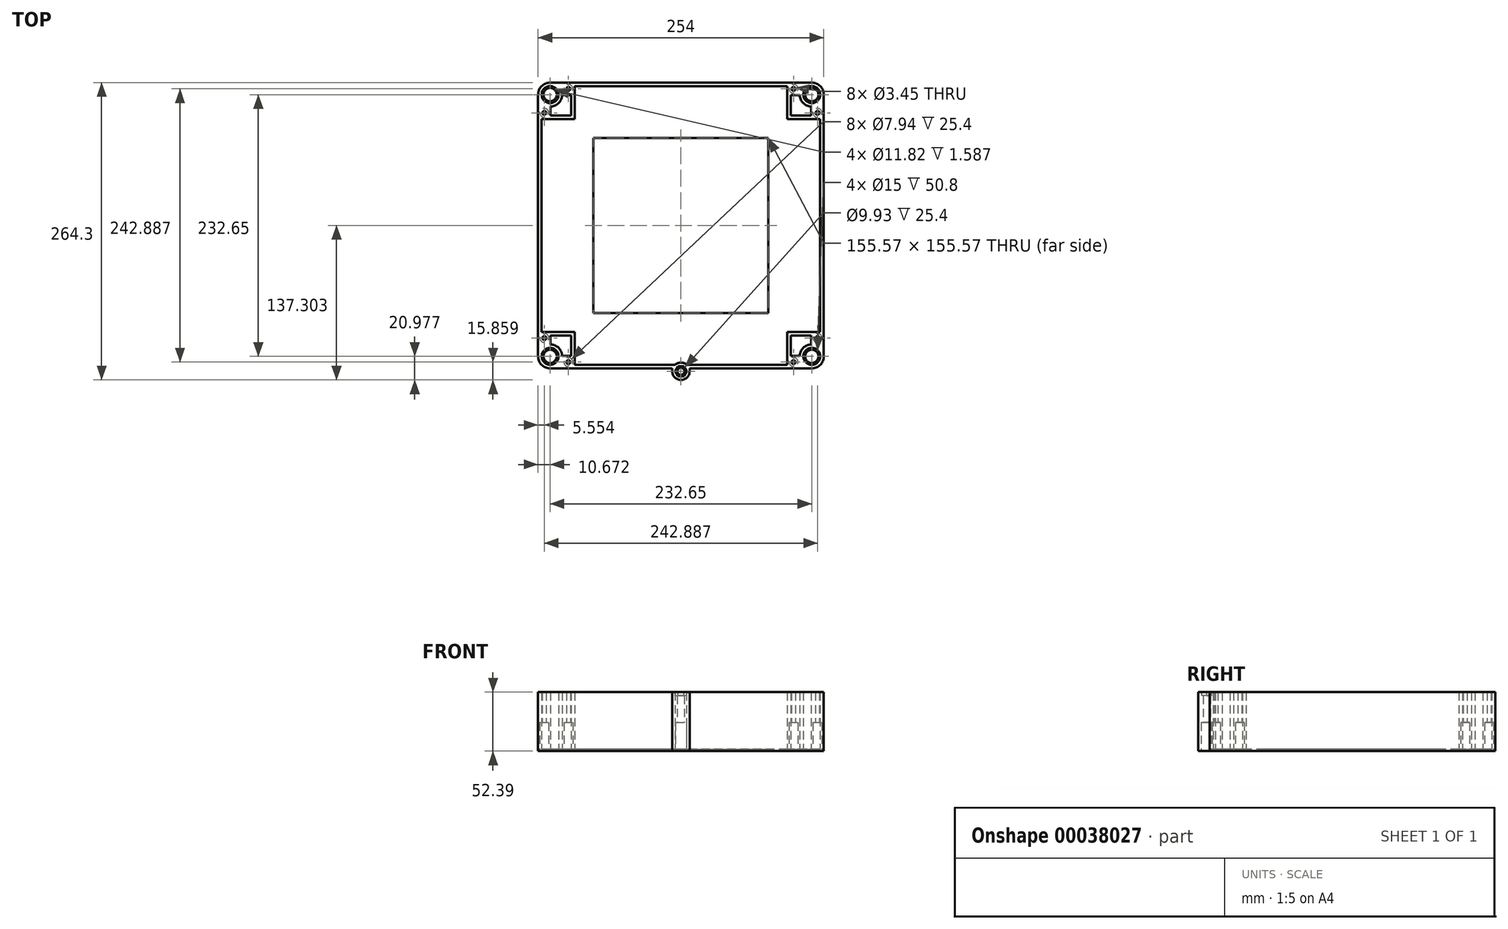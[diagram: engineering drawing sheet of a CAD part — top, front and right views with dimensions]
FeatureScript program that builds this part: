
annotation { "Feature Type Name" : "Feature", "Feature Type Description" : "" }
export const myFeature = defineFeature(function(context is Context, id is Id, definition is map)
    precondition{}
    {
        {
            var Q0;
            Q0=qCreatedBy(makeId("Top.planeOp"),FACE);
            var sketch = newSketch(context, id + "F0", { "sketchPlane" : qUnion([Q0])});
            skLineSegment(sketch, "E0.bottom", {"start": v(0, 0) * mm, "end": v(155.58, 0) * mm});
            skLineSegment(sketch, "E0.top", {"start": v(0, -155.58) * mm, "end": v(155.58, -155.58) * mm});
            skLineSegment(sketch, "E0.left", {"start": v(0, 0) * mm, "end": v(0, -155.58) * mm});
            skLineSegment(sketch, "E0.right", {"start": v(155.58, 0) * mm, "end": v(155.58, -155.58) * mm});
            skLineSegment(sketch, "E1", {"start": v(77.79, -155.58) * mm, "end": v(77.79, 0) * mm, "construction": true});
            skPoint(sketch, "E2.rect.middle", {"position": v(77.79, -77.79) * mm});
            skLineSegment(sketch, "E3.rect.bottom", {"start": v(204.79, 49.21) * mm, "end": v(-49.21, 49.21) * mm});
            skLineSegment(sketch, "E3.rect.top", {"start": v(204.79, -204.79) * mm, "end": v(-49.21, -204.79) * mm});
            skLineSegment(sketch, "E3.rect.left", {"start": v(204.79, 49.21) * mm, "end": v(204.79, -204.79) * mm});
            skLineSegment(sketch, "E3.rect.right", {"start": v(-49.21, 49.21) * mm, "end": v(-49.21, -204.79) * mm});
            skCircle(sketch, "E4", {"center": v(194.11, 38.54) * mm, "radius": 10.67 * mm, "construction": true});
            skCircle(sketch, "E5", {"center": v(-38.54, 38.54) * mm, "radius": 5.91 * mm});
            skCircle(sketch, "E6", {"center": v(-38.54, -194.11) * mm, "radius": 5.91 * mm});
            skCircle(sketch, "E7", {"center": v(194.11, -194.11) * mm, "radius": 5.91 * mm});
            skCircle(sketch, "E8", {"center": v(194.11, 38.54) * mm, "radius": 5.91 * mm});
            skLineSegment(sketch, "E9", {"start": v(77.79, 0) * mm, "end": v(77.79, 38.54) * mm, "construction": true});
            skLineSegment(sketch, "E10", {"start": v(194.11, 38.54) * mm, "end": v(194.11, 22.3) * mm, "construction": true});
            skLineSegment(sketch, "E11", {"start": v(194.11, 38.54) * mm, "end": v(177.88, 38.54) * mm, "construction": true});
            skLineSegment(sketch, "E12", {"start": v(177.88, 38.54) * mm, "end": v(-22.3, 38.54) * mm, "construction": true});
            skLineSegment(sketch, "E13", {"start": v(-22.3, 38.54) * mm, "end": v(-38.54, 38.54) * mm, "construction": true});
            skLineSegment(sketch, "E14", {"start": v(-38.54, 38.54) * mm, "end": v(-38.54, 22.3) * mm, "construction": true});
            skLineSegment(sketch, "E15", {"start": v(-38.54, 22.3) * mm, "end": v(-38.54, -177.88) * mm, "construction": true});
            skLineSegment(sketch, "E16", {"start": v(-38.54, -177.88) * mm, "end": v(-38.54, -194.11) * mm, "construction": true});
            skLineSegment(sketch, "E17", {"start": v(-38.54, -194.11) * mm, "end": v(-22.3, -194.11) * mm, "construction": true});
            skLineSegment(sketch, "E18", {"start": v(-22.3, -194.11) * mm, "end": v(177.88, -194.11) * mm, "construction": true});
            skLineSegment(sketch, "E19", {"start": v(177.88, -194.11) * mm, "end": v(194.11, -194.11) * mm, "construction": true});
            skLineSegment(sketch, "E20", {"start": v(194.11, -194.11) * mm, "end": v(194.11, -177.88) * mm, "construction": true});
            skLineSegment(sketch, "E21", {"start": v(194.11, -177.88) * mm, "end": v(194.11, 22.3) * mm, "construction": true});
            skLineSegment(sketch, "E22", {"start": v(194.11, 22.3) * mm, "end": v(199.23, 22.3) * mm, "construction": true});
            skLineSegment(sketch, "E23", {"start": v(177.88, 38.54) * mm, "end": v(177.88, 43.66) * mm, "construction": true});
            skLineSegment(sketch, "E24", {"start": v(-38.54, 22.3) * mm, "end": v(-43.66, 22.3) * mm, "construction": true});
            skLineSegment(sketch, "E25", {"start": v(-22.3, 38.54) * mm, "end": v(-22.3, 43.66) * mm, "construction": true});
            skLineSegment(sketch, "E26", {"start": v(-38.54, -177.88) * mm, "end": v(-43.66, -177.88) * mm, "construction": true});
            skLineSegment(sketch, "E27", {"start": v(-22.3, -194.11) * mm, "end": v(-22.3, -199.23) * mm, "construction": true});
            skLineSegment(sketch, "E28", {"start": v(177.88, -194.11) * mm, "end": v(177.88, -199.23) * mm, "construction": true});
            skLineSegment(sketch, "E29", {"start": v(194.11, -177.88) * mm, "end": v(199.23, -177.88) * mm, "construction": true});
            skCircle(sketch, "E30", {"center": v(-22.3, -199.23) * mm, "radius": 1.73 * mm});
            skCircle(sketch, "E31", {"center": v(-43.66, -177.88) * mm, "radius": 1.73 * mm});
            skCircle(sketch, "E32", {"center": v(177.88, -199.23) * mm, "radius": 1.73 * mm});
            skCircle(sketch, "E33", {"center": v(199.23, -177.88) * mm, "radius": 1.73 * mm});
            skCircle(sketch, "E34", {"center": v(199.23, 22.3) * mm, "radius": 1.73 * mm});
            skCircle(sketch, "E35", {"center": v(177.88, 43.66) * mm, "radius": 1.73 * mm});
            skCircle(sketch, "E36", {"center": v(-22.3, 43.66) * mm, "radius": 1.73 * mm});
            skCircle(sketch, "E37", {"center": v(-43.66, 22.3) * mm, "radius": 1.73 * mm});
            skLineSegment(sketch, "E38", {"start": v(77.79, -204.79) * mm, "end": v(77.79, -207.4) * mm, "construction": true});
            skLineSegment(sketch, "E39", {"start": v(70.1, -207.4) * mm, "end": v(85.48, -207.4) * mm, "construction": true});
            skCircle(sketch, "E40", {"center": v(77.79, -207.4) * mm, "radius": 3.18 * mm});
            skArc(sketch, "E41", {"start": v(85.48, -207.4) * mm, "mid": v(77.79, -199.7) * mm, "end": v(70.1, -207.4) * mm, "construction": true});
            skLineSegment(sketch, "E42", {"start": v(77.79, -204.79) * mm, "end": v(77.79, -199.7) * mm, "construction": true});
            skLineSegment(sketch, "E43", {"start": v(70.1, -207.4) * mm, "end": v(70.1, -204.79) * mm});
            skLineSegment(sketch, "E44", {"start": v(85.48, -207.4) * mm, "end": v(85.48, -204.79) * mm});
            skArc(sketch, "E45", {"start": v(70.1, -207.4) * mm, "mid": v(77.79, -215.1) * mm, "end": v(85.48, -207.4) * mm});
            skSolve(sketch);
        }
        {
            var Q0;
            Q0 = qSketchRegion(id + "F0", true);
            extrude(context, id + "F1", {"entities" : qUnion([Q0]), "depth" : 1.59 * mm});
        }
        {
            var Q0;
            Q0=makeQuery(id+"F1.opExtrude","CAP_FACE",FACE,{"disambiguationData":[OSD([sQuery(id+"F0.wireOp",EDGE,"E0.bottom"),sQuery(id+"F0.wireOp",EDGE,"E0.top"),sQuery(id+"F0.wireOp",EDGE,"E0.left"),sQuery(id+"F0.wireOp",EDGE,"E0.right"),sQuery(id+"F0.wireOp",EDGE,"E3.rect.bottom"),sQuery(id+"F0.wireOp",EDGE,"E3.rect.top"),sQuery(id+"F0.wireOp",EDGE,"E3.rect.left"),sQuery(id+"F0.wireOp",EDGE,"E3.rect.right"),sQuery(id+"F0.wireOp",EDGE,"E5"),sQuery(id+"F0.wireOp",EDGE,"E6"),sQuery(id+"F0.wireOp",EDGE,"E7"),sQuery(id+"F0.wireOp",EDGE,"E8"),sQuery(id+"F0.wireOp",EDGE,"43b1e4d8-dc6b-47d4-afa9-39d73305b24d"),sQuery(id+"F0.wireOp",EDGE,"f6cbb305-d163-4643-bee7-746698ecbea6"),sQuery(id+"F0.wireOp",EDGE,"d3adae85-02bf-45b9-a1e7-f1405657d824"),sQuery(id+"F0.wireOp",EDGE,"c2a7c8b4-6c69-4894-a4e0-b23b3878c01f"),sQuery(id+"F0.wireOp",EDGE,"fd5b1bc6-ad7d-40a0-8725-81bf3ed5f793"),sQuery(id+"F0.wireOp",EDGE,"3342989b-8784-4d44-b616-02abcfacb7a4"),sQuery(id+"F0.wireOp",EDGE,"51ad0ca2-9e39-4300-82ec-fa5dff985d1e"),sQuery(id+"F0.wireOp",EDGE,"bdff3714-a2b8-41a3-9f31-29bf1a054880")])],"isStart":false});
            var sketch = newSketch(context, id + "F2", { "sketchPlane" : qUnion([Q0])});
            skLineSegment(sketch, "E46.bottom", {"start": v(204.79, 49.21) * mm, "end": v(-49.21, 49.21) * mm});
            skLineSegment(sketch, "E46.top", {"start": v(204.79, -204.79) * mm, "end": v(-49.21, -204.79) * mm});
            skLineSegment(sketch, "E46.left", {"start": v(204.79, 49.21) * mm, "end": v(204.79, -204.79) * mm});
            skLineSegment(sketch, "E46.right", {"start": v(-49.21, 49.21) * mm, "end": v(-49.21, -204.79) * mm});
            skLineSegment(sketch, "E47.bottom", {"start": v(172.33, 46.04) * mm, "end": v(-16.75, 46.04) * mm});
            skLineSegment(sketch, "E47.left", {"start": v(172.33, 46.04) * mm, "end": v(172.33, 16.75) * mm});
            skLineSegment(sketch, "E47.right", {"start": v(-16.75, 46.04) * mm, "end": v(-16.75, 16.75) * mm});
            skLineSegment(sketch, "E48.bottom", {"start": v(201.61, 16.75) * mm, "end": v(172.33, 16.75) * mm});
            skLineSegment(sketch, "E48.top", {"start": v(201.61, -172.33) * mm, "end": v(172.33, -172.33) * mm});
            skLineSegment(sketch, "E48.left", {"start": v(201.61, 16.75) * mm, "end": v(201.61, -172.33) * mm});
            skLineSegment(sketch, "E49", {"start": v(199.23, 22.3) * mm, "end": v(199.23, 16.75) * mm, "construction": true});
            skLineSegment(sketch, "E50", {"start": v(177.88, 43.66) * mm, "end": v(172.33, 43.66) * mm, "construction": true});
            skLineSegment(sketch, "E51", {"start": v(204.79, -77.79) * mm, "end": v(201.61, -77.79) * mm, "construction": true});
            skLineSegment(sketch, "E52", {"start": v(77.79, 49.21) * mm, "end": v(77.79, 46.04) * mm, "construction": true});
            skLineSegment(sketch, "E53", {"start": v(77.79, -204.79) * mm, "end": v(77.79, -201.61) * mm, "construction": true});
            skLineSegment(sketch, "E54", {"start": v(-49.21, -77.79) * mm, "end": v(-46.04, -77.79) * mm, "construction": true});
            skLineSegment(sketch, "E55.top", {"start": v(172.33, -201.61) * mm, "end": v(-16.75, -201.61) * mm});
            skLineSegment(sketch, "E55.left", {"start": v(172.33, -172.33) * mm, "end": v(172.33, -201.61) * mm});
            skLineSegment(sketch, "E55.right", {"start": v(-16.75, -172.33) * mm, "end": v(-16.75, -201.61) * mm});
            skLineSegment(sketch, "E56.bottom", {"start": v(-16.75, 16.75) * mm, "end": v(-46.04, 16.75) * mm});
            skLineSegment(sketch, "E56.top", {"start": v(-16.75, -172.33) * mm, "end": v(-46.04, -172.33) * mm});
            skLineSegment(sketch, "E56.right", {"start": v(-46.04, 16.75) * mm, "end": v(-46.04, -172.33) * mm});
            skLineSegment(sketch, "E57", {"start": v(-22.3, -199.23) * mm, "end": v(-16.75, -199.23) * mm, "construction": true});
            skLineSegment(sketch, "E58", {"start": v(-43.66, -177.88) * mm, "end": v(-43.66, -172.33) * mm, "construction": true});
            skCircle(sketch, "E59", {"center": v(194.11, -194.11) * mm, "radius": 7.5 * mm});
            skCircle(sketch, "E60", {"center": v(194.11, 38.54) * mm, "radius": 7.5 * mm});
            skCircle(sketch, "E61", {"center": v(-38.54, 38.54) * mm, "radius": 7.5 * mm});
            skCircle(sketch, "E62", {"center": v(-38.54, -194.11) * mm, "radius": 7.5 * mm});
            skLineSegment(sketch, "E63", {"start": v(175.5, -172.33) * mm, "end": v(175.5, -175.5) * mm, "construction": true});
            skLineSegment(sketch, "E64", {"start": v(175.5, -175.5) * mm, "end": v(172.33, -175.5) * mm, "construction": true});
            skLineSegment(sketch, "E65", {"start": v(-16.75, 19.93) * mm, "end": v(-19.93, 19.93) * mm, "construction": true});
            skLineSegment(sketch, "E66", {"start": v(-19.93, 19.93) * mm, "end": v(-19.93, 16.75) * mm, "construction": true});
            skLineSegment(sketch, "E67.bottom", {"start": v(175.5, -175.5) * mm, "end": v(193.68, -175.5) * mm});
            skLineSegment(sketch, "E67.top", {"start": v(175.5, -193.68) * mm, "end": v(183.45, -193.68) * mm});
            skLineSegment(sketch, "E67.left", {"start": v(175.5, -175.5) * mm, "end": v(175.5, -193.68) * mm});
            skLineSegment(sketch, "E67.right", {"start": v(193.68, -175.5) * mm, "end": v(193.68, -183.45) * mm});
            skLineSegment(sketch, "E68.bottom", {"start": v(-19.93, 19.93) * mm, "end": v(-38.1, 19.93) * mm});
            skLineSegment(sketch, "E68.top", {"start": v(-19.93, 38.1) * mm, "end": v(-27.87, 38.1) * mm});
            skLineSegment(sketch, "E68.left", {"start": v(-19.93, 19.93) * mm, "end": v(-19.93, 38.1) * mm});
            skLineSegment(sketch, "E68.right", {"start": v(-38.1, 19.93) * mm, "end": v(-38.1, 27.87) * mm});
            skCircle(sketch, "E69", {"center": v(199.23, -177.88) * mm, "radius": 5.56 * mm, "construction": true});
            skArc(sketch, "E70", {"start": v(193.68, -183.45) * mm, "mid": v(186.56, -186.56) * mm, "end": v(183.45, -193.68) * mm});
            skArc(sketch, "E71", {"start": v(-38.1, 27.87) * mm, "mid": v(-30.99, 30.99) * mm, "end": v(-27.87, 38.1) * mm});
            skLineSegment(sketch, "E72.bottom", {"start": v(175.5, 19.93) * mm, "end": v(193.68, 19.93) * mm});
            skLineSegment(sketch, "E72.top", {"start": v(175.5, 38.1) * mm, "end": v(183.45, 38.1) * mm});
            skLineSegment(sketch, "E72.left", {"start": v(175.5, 19.93) * mm, "end": v(175.5, 38.1) * mm});
            skLineSegment(sketch, "E72.right", {"start": v(193.68, 19.93) * mm, "end": v(193.68, 27.87) * mm});
            skArc(sketch, "E73", {"start": v(183.45, 38.1) * mm, "mid": v(186.56, 30.99) * mm, "end": v(193.68, 27.87) * mm});
            skLineSegment(sketch, "E74.bottom", {"start": v(-19.93, -175.5) * mm, "end": v(-38.1, -175.5) * mm});
            skLineSegment(sketch, "E74.top", {"start": v(-19.93, -193.68) * mm, "end": v(-27.87, -193.68) * mm});
            skLineSegment(sketch, "E74.left", {"start": v(-19.93, -175.5) * mm, "end": v(-19.93, -193.68) * mm});
            skLineSegment(sketch, "E74.right", {"start": v(-38.1, -175.5) * mm, "end": v(-38.1, -183.45) * mm});
            skArc(sketch, "E75", {"start": v(-27.87, -193.68) * mm, "mid": v(-30.99, -186.56) * mm, "end": v(-38.1, -183.45) * mm});
            skArc(sketch, "E76", {"start": v(82.86, -201.61) * mm, "mid": v(77.79, -199.7) * mm, "end": v(72.71, -201.61) * mm});
            skLineSegment(sketch, "E77", {"start": v(70.1, -207.4) * mm, "end": v(70.1, -204.79) * mm});
            skLineSegment(sketch, "E78", {"start": v(85.48, -207.4) * mm, "end": v(85.48, -204.79) * mm});
            skArc(sketch, "E79", {"start": v(70.1, -207.4) * mm, "mid": v(77.79, -215.1) * mm, "end": v(85.48, -207.4) * mm});
            skSolve(sketch);
        }
        {
            var Q0;
            Q0=makeQuery(id+"F2.imprint","IMPRINT",FACE,{"disambiguationData":[TD([[makeQuery(id+"F2.imprint","IMPRINT",EDGE,{"derivedFrom":sQuery(id+"F2.wireOp",EDGE,"E46.bottom")}),1.0]])]});
            var Q1;
            {var subQ0=sQuery(id+"F2.wireOp",EDGE,"E77");Q1=makeQuery(id+"F2.imprint","IMPRINT",FACE,{"disambiguationData":[TD([[makeQuery(id+"F2.imprint","IMPRINT",EDGE,{"derivedFrom":subQ0}),-1.0]])]});}
            var Q2;
            {var subQ0=sQuery(id+"F2.wireOp",EDGE,"E76");Q2=makeQuery(id+"F2.imprint","IMPRINT",FACE,{"disambiguationData":[TD([[makeQuery(id+"F2.imprint","IMPRINT",EDGE,{"derivedFrom":subQ0}),1.0]])]});}
            extrude(context, id + "F3", {"entities" : qUnion([Q0, Q1, Q2]), "operationType" : NewBodyOperationType.ADD, "depth" : 50.8 * mm});
        }
        {
            var Q0;
            Q0=makeQuery(id+"F1.opExtrude","CAP_FACE",FACE,{"disambiguationData":[OSD([sQuery(id+"F0.wireOp",EDGE,"E0.bottom"),sQuery(id+"F0.wireOp",EDGE,"E0.top"),sQuery(id+"F0.wireOp",EDGE,"E0.left"),sQuery(id+"F0.wireOp",EDGE,"E0.right"),sQuery(id+"F0.wireOp",EDGE,"E3.rect.bottom"),sQuery(id+"F0.wireOp",EDGE,"E3.rect.top"),sQuery(id+"F0.wireOp",EDGE,"E3.rect.left"),sQuery(id+"F0.wireOp",EDGE,"E3.rect.right"),sQuery(id+"F0.wireOp",EDGE,"E5"),sQuery(id+"F0.wireOp",EDGE,"E6"),sQuery(id+"F0.wireOp",EDGE,"E7"),sQuery(id+"F0.wireOp",EDGE,"E8"),sQuery(id+"F0.wireOp",EDGE,"E30"),sQuery(id+"F0.wireOp",EDGE,"E31"),sQuery(id+"F0.wireOp",EDGE,"E32"),sQuery(id+"F0.wireOp",EDGE,"E33"),sQuery(id+"F0.wireOp",EDGE,"E34"),sQuery(id+"F0.wireOp",EDGE,"E35"),sQuery(id+"F0.wireOp",EDGE,"E36"),sQuery(id+"F0.wireOp",EDGE,"E37")])],"isStart":true});
            var sketch = newSketch(context, id + "F4", { "sketchPlane" : qUnion([Q0])});
            skCircle(sketch, "E80", {"center": v(-43.66, -22.3) * mm, "radius": 3.97 * mm});
            skCircle(sketch, "E81", {"center": v(-22.3, -43.66) * mm, "radius": 3.97 * mm});
            skCircle(sketch, "E82", {"center": v(-43.66, 177.88) * mm, "radius": 3.97 * mm});
            skCircle(sketch, "E83", {"center": v(-22.3, 199.23) * mm, "radius": 3.97 * mm});
            skCircle(sketch, "E84", {"center": v(199.23, 177.88) * mm, "radius": 3.97 * mm});
            skCircle(sketch, "E85", {"center": v(177.88, 199.23) * mm, "radius": 3.97 * mm});
            skCircle(sketch, "E86", {"center": v(177.88, -43.66) * mm, "radius": 3.97 * mm});
            skCircle(sketch, "E87", {"center": v(199.23, -22.3) * mm, "radius": 3.97 * mm});
            skSolve(sketch);
        }
        {
            var Q0;
            Q0 = qSketchRegion(id + "F4", true);
            extrude(context, id + "F5", {"entities" : qUnion([Q0]), "operationType" : NewBodyOperationType.REMOVE, "oppositeDirection" : true, "depth" : 25.4 * mm});
        }
        {
            var Q0;
            Q0=makeQuery(id+"F3.boolean.opBoolean","MERGE",EDGE,{"derivedFrom":[makeQuery(id+"F1.opExtrude","SWEPT_EDGE",EDGE,{"disambiguationData":[OSD([sQuery(id+"F0.wireOp",EDGE,"E3.rect.bottom"),sQuery(id+"F0.wireOp",EDGE,"E3.rect.left")])]}),makeQuery(id+"F3.opExtrude","SWEPT_EDGE",EDGE,{"disambiguationData":[OSD([sQuery(id+"F2.wireOp",EDGE,"E46.bottom"),sQuery(id+"F2.wireOp",EDGE,"E46.left")])]})]});
            var Q1;
            Q1=makeQuery(id+"F3.boolean.opBoolean","MERGE",EDGE,{"derivedFrom":[makeQuery(id+"F1.opExtrude","SWEPT_EDGE",EDGE,{"disambiguationData":[OSD([sQuery(id+"F0.wireOp",EDGE,"E3.rect.top"),sQuery(id+"F0.wireOp",EDGE,"E3.rect.left")])]}),makeQuery(id+"F3.opExtrude","SWEPT_EDGE",EDGE,{"disambiguationData":[OSD([sQuery(id+"F2.wireOp",EDGE,"E46.top"),sQuery(id+"F2.wireOp",EDGE,"E46.left")])]})]});
            var Q2;
            Q2=makeQuery(id+"F3.boolean.opBoolean","MERGE",EDGE,{"derivedFrom":[makeQuery(id+"F1.opExtrude","SWEPT_EDGE",EDGE,{"disambiguationData":[OSD([sQuery(id+"F0.wireOp",EDGE,"E3.rect.top"),sQuery(id+"F0.wireOp",EDGE,"E3.rect.right")])]}),makeQuery(id+"F3.opExtrude","SWEPT_EDGE",EDGE,{"disambiguationData":[OSD([sQuery(id+"F2.wireOp",EDGE,"E46.top"),sQuery(id+"F2.wireOp",EDGE,"E46.right")])]})]});
            var Q3;
            Q3=makeQuery(id+"F3.boolean.opBoolean","MERGE",EDGE,{"derivedFrom":[makeQuery(id+"F1.opExtrude","SWEPT_EDGE",EDGE,{"disambiguationData":[OSD([sQuery(id+"F0.wireOp",EDGE,"E3.rect.bottom"),sQuery(id+"F0.wireOp",EDGE,"E3.rect.right")])]}),makeQuery(id+"F3.opExtrude","SWEPT_EDGE",EDGE,{"disambiguationData":[OSD([sQuery(id+"F2.wireOp",EDGE,"E46.bottom"),sQuery(id+"F2.wireOp",EDGE,"E46.right")])]})]});
            fillet(context, id + "F6", {"entities" : qUnion([Q0, Q1, Q2, Q3]), "radius" : 10.67 * mm, "tangentPropagation" : true, "allowEdgeOverflow" : false});
        }
        {
            var Q0;
            Q0=makeQuery(id+"F1.opExtrude","CAP_FACE",FACE,{"disambiguationData":[OSD([sQuery(id+"F0.wireOp",EDGE,"E0.bottom"),sQuery(id+"F0.wireOp",EDGE,"E0.top"),sQuery(id+"F0.wireOp",EDGE,"E0.left"),sQuery(id+"F0.wireOp",EDGE,"E0.right"),sQuery(id+"F0.wireOp",EDGE,"E3.rect.bottom"),sQuery(id+"F0.wireOp",EDGE,"E3.rect.top"),sQuery(id+"F0.wireOp",EDGE,"E3.rect.left"),sQuery(id+"F0.wireOp",EDGE,"E3.rect.right"),sQuery(id+"F0.wireOp",EDGE,"E5"),sQuery(id+"F0.wireOp",EDGE,"E6"),sQuery(id+"F0.wireOp",EDGE,"E7"),sQuery(id+"F0.wireOp",EDGE,"E8"),sQuery(id+"F0.wireOp",EDGE,"E30"),sQuery(id+"F0.wireOp",EDGE,"E31"),sQuery(id+"F0.wireOp",EDGE,"E32"),sQuery(id+"F0.wireOp",EDGE,"E33"),sQuery(id+"F0.wireOp",EDGE,"E34"),sQuery(id+"F0.wireOp",EDGE,"E35"),sQuery(id+"F0.wireOp",EDGE,"E36"),sQuery(id+"F0.wireOp",EDGE,"E37"),sQuery(id+"F0.wireOp",EDGE,"E40"),sQuery(id+"F0.wireOp",EDGE,"E43"),sQuery(id+"F0.wireOp",EDGE,"E44"),sQuery(id+"F0.wireOp",EDGE,"E45")])],"isStart":true});
            var sketch = newSketch(context, id + "F7", { "sketchPlane" : qUnion([Q0])});
            skCircle(sketch, "E88", {"center": v(77.79, 207.4) * mm, "radius": 4.96 * mm});
            skSolve(sketch);
        }
        {
            var Q0;
            Q0=makeQuery(id+"F3.opExtrude","CAP_FACE",FACE,{"disambiguationData":[OSD([sQuery(id+"F0.wireOp",EDGE,"E30"),sQuery(id+"F0.wireOp",EDGE,"E31"),sQuery(id+"F0.wireOp",EDGE,"E32"),sQuery(id+"F0.wireOp",EDGE,"E33"),sQuery(id+"F0.wireOp",EDGE,"E34"),sQuery(id+"F0.wireOp",EDGE,"E35"),sQuery(id+"F0.wireOp",EDGE,"E36"),sQuery(id+"F0.wireOp",EDGE,"E37"),sQuery(id+"F0.wireOp",EDGE,"E40"),sQuery(id+"F2.wireOp",EDGE,"E46.bottom"),sQuery(id+"F2.wireOp",EDGE,"E46.top"),sQuery(id+"F2.wireOp",EDGE,"E46.left"),sQuery(id+"F2.wireOp",EDGE,"E46.right"),sQuery(id+"F2.wireOp",EDGE,"E47.bottom"),sQuery(id+"F2.wireOp",EDGE,"E47.left"),sQuery(id+"F2.wireOp",EDGE,"E47.right"),sQuery(id+"F2.wireOp",EDGE,"E48.bottom"),sQuery(id+"F2.wireOp",EDGE,"E48.top"),sQuery(id+"F2.wireOp",EDGE,"E48.left"),sQuery(id+"F2.wireOp",EDGE,"E55.top"),sQuery(id+"F2.wireOp",EDGE,"E55.left"),sQuery(id+"F2.wireOp",EDGE,"E55.right"),sQuery(id+"F2.wireOp",EDGE,"E56.bottom"),sQuery(id+"F2.wireOp",EDGE,"E56.top"),sQuery(id+"F2.wireOp",EDGE,"E56.right"),sQuery(id+"F2.wireOp",EDGE,"E59"),sQuery(id+"F2.wireOp",EDGE,"E60"),sQuery(id+"F2.wireOp",EDGE,"E61"),sQuery(id+"F2.wireOp",EDGE,"E62"),sQuery(id+"F2.wireOp",EDGE,"E67.bottom"),sQuery(id+"F2.wireOp",EDGE,"E67.top"),sQuery(id+"F2.wireOp",EDGE,"E67.left"),sQuery(id+"F2.wireOp",EDGE,"E67.right"),sQuery(id+"F2.wireOp",EDGE,"E68.bottom"),sQuery(id+"F2.wireOp",EDGE,"E68.top"),sQuery(id+"F2.wireOp",EDGE,"E68.left"),sQuery(id+"F2.wireOp",EDGE,"E68.right"),sQuery(id+"F2.wireOp",EDGE,"E70"),sQuery(id+"F2.wireOp",EDGE,"E71"),sQuery(id+"F2.wireOp",EDGE,"E72.bottom"),sQuery(id+"F2.wireOp",EDGE,"E72.top"),sQuery(id+"F2.wireOp",EDGE,"E72.left"),sQuery(id+"F2.wireOp",EDGE,"E72.right"),sQuery(id+"F2.wireOp",EDGE,"E73"),sQuery(id+"F2.wireOp",EDGE,"E74.bottom"),sQuery(id+"F2.wireOp",EDGE,"E74.top"),sQuery(id+"F2.wireOp",EDGE,"E74.left"),sQuery(id+"F2.wireOp",EDGE,"E74.right"),sQuery(id+"F2.wireOp",EDGE,"E75"),sQuery(id+"F2.wireOp",EDGE,"E76"),sQuery(id+"F2.wireOp",EDGE,"E77"),sQuery(id+"F2.wireOp",EDGE,"E78"),sQuery(id+"F2.wireOp",EDGE,"E79")])],"isStart":false});
            var sketch = newSketch(context, id + "F8", { "sketchPlane" : qUnion([Q0])});
            skCircle(sketch, "E89.cCircle", {"center": v(77.79, -207.4) * mm, "radius": 4.52 * mm, "construction": true});
            skLineSegment(sketch, "E89.0", {"start": v(80.4, -211.92) * mm, "end": v(75.18, -211.92) * mm});
            skLineSegment(sketch, "E89.1", {"start": v(75.18, -211.92) * mm, "end": v(72.57, -207.4) * mm});
            skLineSegment(sketch, "E89.2", {"start": v(72.57, -207.4) * mm, "end": v(75.18, -202.87) * mm});
            skLineSegment(sketch, "E89.3", {"start": v(75.18, -202.87) * mm, "end": v(80.4, -202.87) * mm});
            skLineSegment(sketch, "E89.4", {"start": v(80.4, -202.87) * mm, "end": v(83, -207.4) * mm});
            skLineSegment(sketch, "E89.5", {"start": v(83, -207.4) * mm, "end": v(80.4, -211.92) * mm});
            skPoint(sketch, "E89.0.midPoint", {"position": v(77.79, -211.92) * mm});
            skSolve(sketch);
        }
        {
            var Q0;
            Q0 = qSketchRegion(id + "F8", true);
            extrude(context, id + "F9", {"entities" : qUnion([Q0]), "operationType" : NewBodyOperationType.REMOVE, "oppositeDirection" : true, "depth" : 3.17 * mm});
        }
        {
            var Q0;
            Q0 = qSketchRegion(id + "F7", true);
            extrude(context, id + "F10", {"entities" : qUnion([Q0]), "operationType" : NewBodyOperationType.REMOVE, "oppositeDirection" : true, "depth" : 25.4 * mm});
        }
    });
